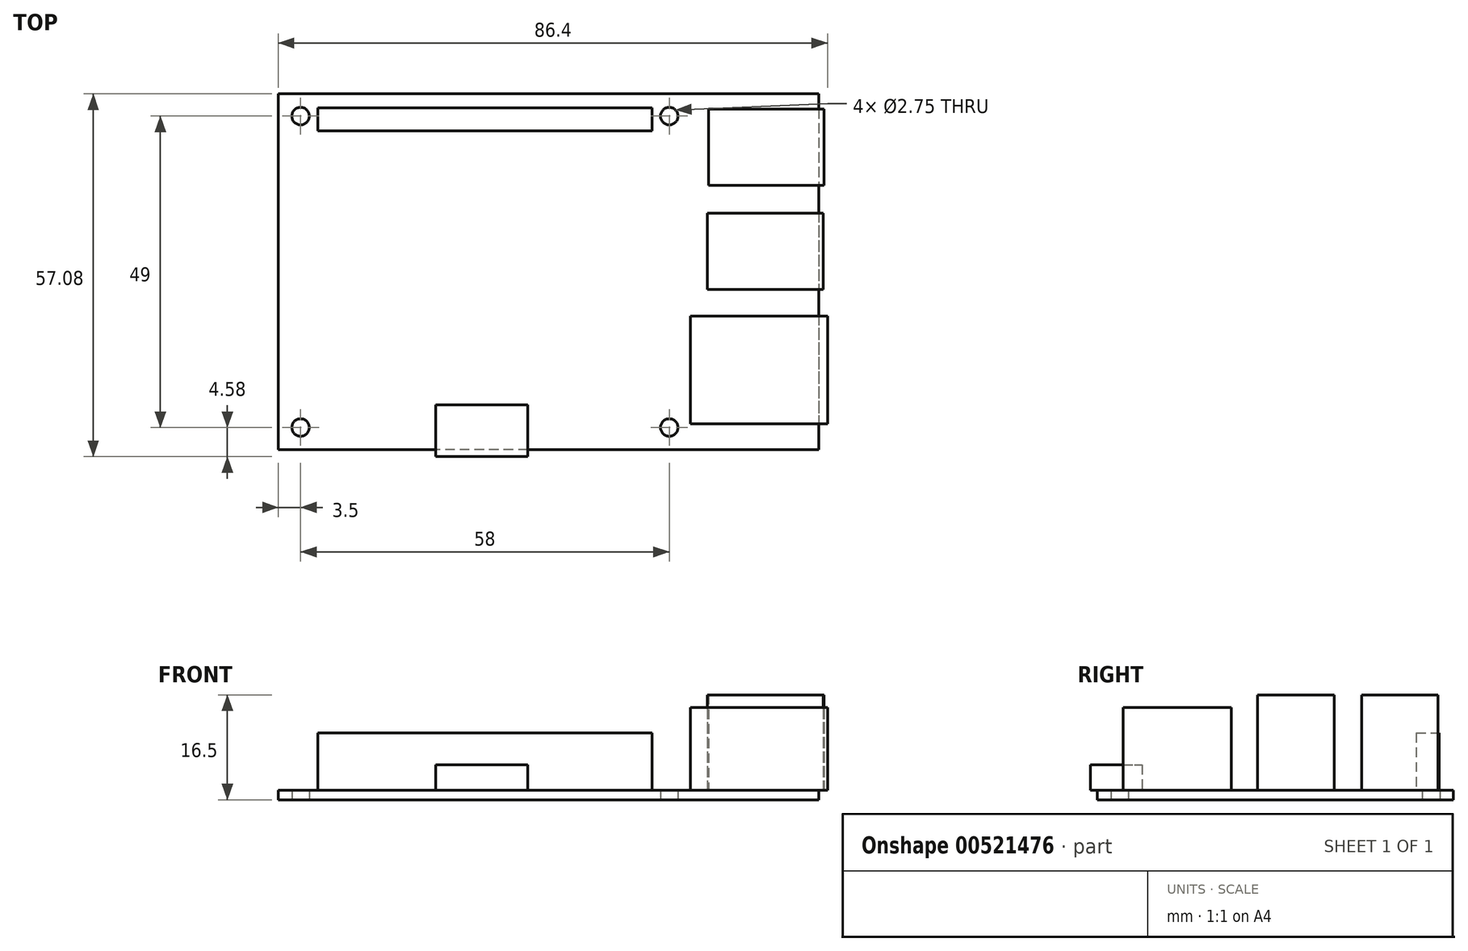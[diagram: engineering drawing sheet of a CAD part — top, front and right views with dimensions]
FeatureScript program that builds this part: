
annotation { "Feature Type Name" : "Feature", "Feature Type Description" : "" }
export const myFeature = defineFeature(function(context is Context, id is Id, definition is map)
    precondition{}
    {
        {
            var Q0;
            Q0=qCreatedBy(makeId("Top.planeOp"),FACE);
            var sketch = newSketch(context, id + "F0", { "sketchPlane" : qUnion([Q0])});
            skLineSegment(sketch, "E0.bottom", {"start": v(42.5, 28) * mm, "end": v(-42.5, 28) * mm});
            skLineSegment(sketch, "E0.top", {"start": v(42.5, -28) * mm, "end": v(-42.5, -28) * mm});
            skLineSegment(sketch, "E0.left", {"start": v(42.5, 28) * mm, "end": v(42.5, -28) * mm});
            skLineSegment(sketch, "E0.right", {"start": v(-42.5, 28) * mm, "end": v(-42.5, -28) * mm});
            skPoint(sketch, "E0.middle", {"position": v(0, 0) * mm});
            skLineSegment(sketch, "E1.bottom", {"start": v(-39, 24.5) * mm, "end": v(19, 24.5) * mm, "construction": true});
            skLineSegment(sketch, "E1.top", {"start": v(-39, -24.5) * mm, "end": v(19, -24.5) * mm, "construction": true});
            skLineSegment(sketch, "E1.left", {"start": v(-39, 24.5) * mm, "end": v(-39, -24.5) * mm, "construction": true});
            skLineSegment(sketch, "E1.right", {"start": v(19, 24.5) * mm, "end": v(19, -24.5) * mm, "construction": true});
            skCircle(sketch, "E2", {"center": v(-39, 24.5) * mm, "radius": 1.38 * mm});
            skCircle(sketch, "E3", {"center": v(19, 24.5) * mm, "radius": 1.38 * mm});
            skCircle(sketch, "E4", {"center": v(19, -24.5) * mm, "radius": 1.38 * mm});
            skCircle(sketch, "E5", {"center": v(-39, -24.5) * mm, "radius": 1.38 * mm});
            skPoint(sketch, "E6", {"position": v(-39, 0) * mm});
            skSolve(sketch);
        }
        {
            var Q0;
            Q0=makeQuery(id+"F0.imprint","IMPRINT",FACE,{"disambiguationData":[TD([[makeQuery(id+"F0.imprint","IMPRINT",EDGE,{"derivedFrom":sQuery(id+"F0.wireOp",EDGE,"E0.bottom")}),1.0]])]});
            extrude(context, id + "F1", {"entities" : qUnion([Q0]), "depth" : 1.5 * mm, "offsetDistance" : 25 * mm});
        }
        {
            var Q0;
            Q0=makeQuery(id+"F1.opExtrude","CAP_FACE",FACE,{"disambiguationData":[OSD([sQuery(id+"F0.wireOp",EDGE,"E0.bottom"),sQuery(id+"F0.wireOp",EDGE,"E0.top"),sQuery(id+"F0.wireOp",EDGE,"E0.left"),sQuery(id+"F0.wireOp",EDGE,"E0.right"),sQuery(id+"F0.wireOp",EDGE,"E2"),sQuery(id+"F0.wireOp",EDGE,"E3"),sQuery(id+"F0.wireOp",EDGE,"E4"),sQuery(id+"F0.wireOp",EDGE,"E5")])],"isStart":false});
            var sketch = newSketch(context, id + "F2", { "sketchPlane" : qUnion([Q0])});
            skLineSegment(sketch, "E7.bottom", {"start": v(-36.26, 22.16) * mm, "end": v(16.3, 22.16) * mm});
            skLineSegment(sketch, "E7.top", {"start": v(-36.26, 25.8) * mm, "end": v(16.3, 25.8) * mm});
            skLineSegment(sketch, "E7.left", {"start": v(-36.26, 22.16) * mm, "end": v(-36.26, 25.8) * mm});
            skLineSegment(sketch, "E7.right", {"start": v(16.3, 22.16) * mm, "end": v(16.3, 25.8) * mm});
            skLineSegment(sketch, "E8.bottom", {"start": v(-17.75, -29.08) * mm, "end": v(-3.25, -29.08) * mm});
            skLineSegment(sketch, "E8.top", {"start": v(-17.75, -20.94) * mm, "end": v(-3.25, -20.94) * mm});
            skLineSegment(sketch, "E8.left", {"start": v(-17.75, -29.08) * mm, "end": v(-17.75, -20.94) * mm});
            skLineSegment(sketch, "E8.right", {"start": v(-3.25, -29.08) * mm, "end": v(-3.25, -20.94) * mm});
            skPoint(sketch, "E8.middle", {"position": v(-10.5, -25.01) * mm});
            skLineSegment(sketch, "E9.bottom", {"start": v(25.18, 25.58) * mm, "end": v(43.37, 25.58) * mm});
            skLineSegment(sketch, "E9.top", {"start": v(25.18, 13.58) * mm, "end": v(43.37, 13.58) * mm});
            skLineSegment(sketch, "E9.left", {"start": v(25.18, 25.58) * mm, "end": v(25.18, 13.58) * mm});
            skLineSegment(sketch, "E9.right", {"start": v(43.37, 25.58) * mm, "end": v(43.37, 13.58) * mm});
            skPoint(sketch, "E9.middle", {"position": v(34.27, 19.58) * mm});
            skLineSegment(sketch, "E10.bottom", {"start": v(43.9, -23.94) * mm, "end": v(22.32, -23.94) * mm});
            skLineSegment(sketch, "E10.top", {"start": v(43.9, -6.95) * mm, "end": v(22.32, -6.95) * mm});
            skLineSegment(sketch, "E10.left", {"start": v(43.9, -23.94) * mm, "end": v(43.9, -6.95) * mm});
            skLineSegment(sketch, "E10.right", {"start": v(22.32, -23.94) * mm, "end": v(22.32, -6.95) * mm});
            skPoint(sketch, "E10.middle", {"position": v(33.1, -15.44) * mm});
            skLineSegment(sketch, "E11.bottom", {"start": v(25, 9.24) * mm, "end": v(43.2, 9.24) * mm});
            skLineSegment(sketch, "E11.top", {"start": v(25, -2.77) * mm, "end": v(43.2, -2.77) * mm});
            skLineSegment(sketch, "E11.left", {"start": v(25, 9.24) * mm, "end": v(25, -2.77) * mm});
            skLineSegment(sketch, "E11.right", {"start": v(43.2, 9.24) * mm, "end": v(43.2, -2.77) * mm});
            skPoint(sketch, "E11.middle", {"position": v(34.1, 3.24) * mm});
            skSolve(sketch);
        }
        {
            var Q0;
            {var subQ0=sQuery(id+"F2.wireOp",EDGE,"E8.top");Q0=makeQuery(id+"F2.imprint","IMPRINT",FACE,{"disambiguationData":[TD([[makeQuery(id+"F2.imprint","IMPRINT",EDGE,{"derivedFrom":subQ0}),-1.0]])]});}
            var Q1;
            {var subQ0=sQuery(id+"F2.wireOp",EDGE,"E8.bottom");Q1=makeQuery(id+"F2.imprint","IMPRINT",FACE,{"disambiguationData":[TD([[makeQuery(id+"F2.imprint","IMPRINT",EDGE,{"derivedFrom":subQ0}),1.0]])]});}
            extrude(context, id + "F3", {"entities" : qUnion([Q0, Q1]), "operationType" : NewBodyOperationType.ADD, "depth" : 4 * mm, "offsetDistance" : 25 * mm});
        }
        {
            var Q0;
            Q0=makeQuery(id+"F2.imprint","IMPRINT",FACE,{"disambiguationData":[TD([[makeQuery(id+"F2.imprint","IMPRINT",EDGE,{"derivedFrom":sQuery(id+"F2.wireOp",EDGE,"E7.bottom")}),1.0]])]});
            extrude(context, id + "F4", {"entities" : qUnion([Q0]), "operationType" : NewBodyOperationType.ADD, "depth" : 9 * mm, "offsetDistance" : 25 * mm});
        }
        {
            var Q0;
            {var subQ0=sQuery(id+"F2.wireOp",EDGE,"E11.right");Q0=makeQuery(id+"F2.imprint","IMPRINT",FACE,{"disambiguationData":[TD([[makeQuery(id+"F2.imprint","IMPRINT",EDGE,{"derivedFrom":subQ0}),-1.0]])]});}
            var Q1;
            {var subQ0=sQuery(id+"F2.wireOp",EDGE,"E11.left");Q1=makeQuery(id+"F2.imprint","IMPRINT",FACE,{"disambiguationData":[TD([[makeQuery(id+"F2.imprint","IMPRINT",EDGE,{"derivedFrom":subQ0}),1.0]])]});}
            var Q2;
            {var subQ0=sQuery(id+"F2.wireOp",EDGE,"E9.right");Q2=makeQuery(id+"F2.imprint","IMPRINT",FACE,{"disambiguationData":[TD([[makeQuery(id+"F2.imprint","IMPRINT",EDGE,{"derivedFrom":subQ0}),-1.0]])]});}
            var Q3;
            {var subQ0=sQuery(id+"F2.wireOp",EDGE,"E9.left");Q3=makeQuery(id+"F2.imprint","IMPRINT",FACE,{"disambiguationData":[TD([[makeQuery(id+"F2.imprint","IMPRINT",EDGE,{"derivedFrom":subQ0}),1.0]])]});}
            extrude(context, id + "F5", {"entities" : qUnion([Q0, Q1, Q2, Q3]), "operationType" : NewBodyOperationType.ADD, "depth" : 15 * mm, "offsetDistance" : 25 * mm});
        }
        {
            var Q0;
            {var subQ0=sQuery(id+"F2.wireOp",EDGE,"E10.right");Q0=makeQuery(id+"F2.imprint","IMPRINT",FACE,{"disambiguationData":[TD([[makeQuery(id+"F2.imprint","IMPRINT",EDGE,{"derivedFrom":subQ0}),-1.0]])]});}
            var Q1;
            {var subQ0=sQuery(id+"F2.wireOp",EDGE,"E10.left");Q1=makeQuery(id+"F2.imprint","IMPRINT",FACE,{"disambiguationData":[TD([[makeQuery(id+"F2.imprint","IMPRINT",EDGE,{"derivedFrom":subQ0}),1.0]])]});}
            extrude(context, id + "F6", {"entities" : qUnion([Q0, Q1]), "operationType" : NewBodyOperationType.ADD, "depth" : 13 * mm, "offsetDistance" : 25 * mm});
        }
    });
